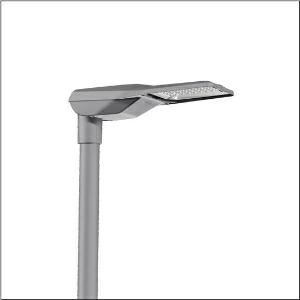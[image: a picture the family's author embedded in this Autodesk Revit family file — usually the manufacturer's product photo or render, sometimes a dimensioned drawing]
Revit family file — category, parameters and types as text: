
# Revit family: streetlight_sl_21_iq_mini___st1_0a_5xe2d21g08hb_8dd2
name_source: partatom
category: Lighting Fixtures
units: mm (PartAtom-declared; Revit-internal decimal feet)

## family parameters
Cut with Voids When Loaded = No
Host = Face
Light Source = No
Part Type = Normal
Room Calculation Point = No
Round Connector Dimension = Use Diameter
Shared = No

## types (1)
- --- (1 x LED, 7830 lm, 70.9 W, 2200K)
    Apparent Load = 71 VA
    CIE Flux Codes = 37 72 97 100 100
    Color Rendering = 70
    Color Temperature = 2200K
    Default Elevation = 1800 mm
    Description = Streetlight SL 21 iQ mini, mast luminaire, primary light control with lens, of PMMA, primary optical cover: cover, of toughened safety glass, transparent, light distribution: ST1.0a, light emission: direct distribution, primary light characteristic: asymmetric, installation type: post-top, side-entry, LED, High Power LED, rated luminous flux: 7.830lm, luminous efficacy: 110lm/W, light colour: 722, colour temperature: 2200K, control: Street-Remote, Auto-Match, Temp-Guard, Lumen-Switch, Night-Set, Smart-Wire, Light-Fading, Desk-Remote (wireless, voltage-free reading and setting of iQ features in the workshop via application-optimized NFC function/RFID function), optimised constant luminous flux control (CLO 2.0), presetting dimming linear, mains connection: 220..240V, AC, 50/60Hz, start of lifetime: 71W, end of service life: 75W, reduction: 31W, luminaire housing, of diecast aluminium, powder-coated, Siteco® metallic grey (DB 702S), corrosivity category C5 mid according to DIN EN ISO 12944, please order mast flange separately, inclination adjustable: 0°, 5°, 10°, 15°, sealing non-destructively replaceable, multi-level sealing system, length: 628mm, width: 235mm, height: 110mm, mast flange for spigot size: 42mm (side-entry): 5XC10008XM4, 60/48mm (side-entry/post-top): 5XC10108XM2, 76/60mm (side-entry/post-top): 5XC10108XM1, protection rating (complete): IP66, insulation class (complete): insulation class II (safety insulation), certification: CE, ENEC, ENEC+, VDE, impact resistance: IK09, permissible operating ambient temperature for outdoor applications: -40..+50°C, standard-compliant lighting for roads and squares, packaging unit: 1 piece

Light Distribution: ST1.0a
    Height = 110 mm
    Lamp = 1 x LED
    Lamp Light Flux = 7830 lm
    Lamp Power = 70.9 W
    Lamp count = 1
    Length = 625 mm
    Luminous efficacy = 110 lm/W
    Manufacturer = Siteco
    ModVariant = No
    Model = 5XE2D21G08HB
    Number of Poles = 1
    OnlyDefault = Yes
    Power Factor = 1
    Product Name = Streetlight SL 21 iQ mini | ST1.0a
    Product group = mast luminaire | pylon top
    ProductGroupID = 6100
    Protection Class = Protection class II
    Protection Degree = IP 66
    RLX_Detail_Level = 1
    RLX_Emergency_Light_Flux = 0 lm
    RLX_Emergency_Type = 0
    RLX_Emergency_Type_DB = No
    RlxData = <blob elided: 92393 chars, md5=90cac35f>
    Socket = socket
    Standby Power = 0 W
    System Light Flux = 7830 lm
    System Power = 71 W
    Type Comments = factory setting: luminous flux: 100 % | dim-lin: 254 | 711 mA
    Type Image = l_1003519.jpg
    URL = http://relux.com
    VarID = @adj_108461
    Voltage = 0 V
    Weight = 0.00 kg
    Width = 234 mm

## geometry (parser evidence)
native form markers: Blend x4, Sweep x11
no freeform markers — native parametric forms only
